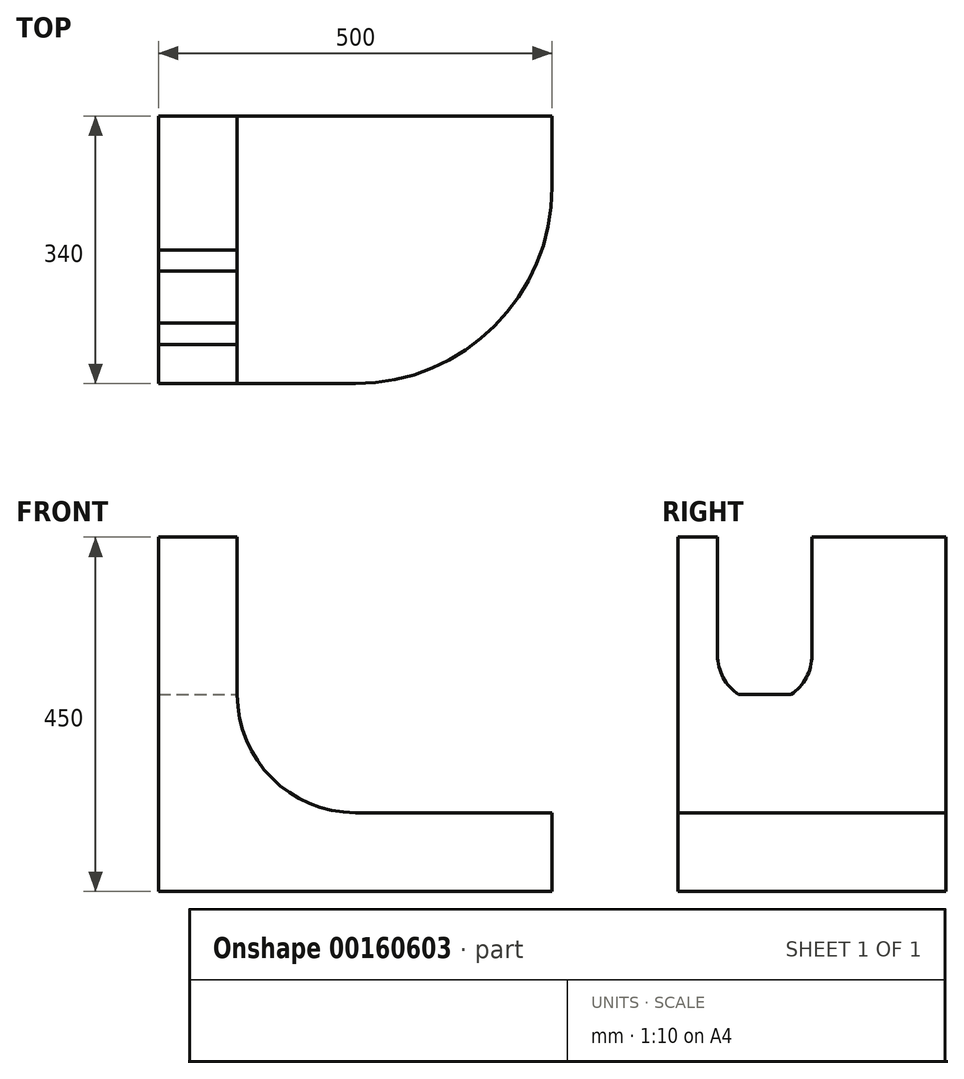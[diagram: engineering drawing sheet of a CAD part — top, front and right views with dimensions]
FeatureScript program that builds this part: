
annotation { "Feature Type Name" : "Feature", "Feature Type Description" : "" }
export const myFeature = defineFeature(function(context is Context, id is Id, definition is map)
    precondition{}
    {
        {
            var Q0;
            Q0=qCreatedBy(makeId("Front.planeOp"),FACE);
            var sketch = newSketch(context, id + "F0", { "sketchPlane" : qUnion([Q0])});
            skLineSegment(sketch, "E0", {"start": v(0, 0) * mm, "end": v(0, 450) * mm});
            skLineSegment(sketch, "E1", {"start": v(0, 0) * mm, "end": v(500, 0) * mm});
            skLineSegment(sketch, "E2.0", {"start": v(250, 100) * mm, "end": v(500, 100) * mm});
            skLineSegment(sketch, "E3.0", {"start": v(100, 250) * mm, "end": v(100, 450) * mm});
            skLineSegment(sketch, "E4", {"start": v(0, 450) * mm, "end": v(100, 450) * mm});
            skLineSegment(sketch, "E5", {"start": v(500, 100) * mm, "end": v(500, 0) * mm});
            skPoint(sketch, "E6.visualSharp", {"position": v(100, 100) * mm});
            skArc(sketch, "E6.filletArc", {"start": v(100, 250) * mm, "mid": v(143.93, 143.93) * mm, "end": v(250, 100) * mm});
            skSolve(sketch);
        }
        {
            var Q0;
            Q0=makeQuery(id+"F0.imprint","IMPRINT",FACE,{"disambiguationData":[TD([[makeQuery(id+"F0.imprint","IMPRINT",EDGE,{"derivedFrom":sQuery(id+"F0.wireOp",EDGE,"E0")}),-1.0]])]});
            extrude(context, id + "F1", {"entities" : qUnion([Q0]), "oppositeDirection" : true, "depth" : 340 * mm});
        }
        {
            var Q0;
            Q0=makeQuery(id+"F1.opExtrude","CAP_EDGE",EDGE,{"disambiguationData":[OSD([sQuery(id+"F0.wireOp",EDGE,"E5")])],"isStart":true});
            fillet(context, id + "F2", {"entities" : qUnion([Q0]), "radius" : 250 * mm, "tangentPropagation" : true, "allowEdgeOverflow" : false});
        }
        {
            var Q0;
            Q0=makeQuery(id+"F1.opExtrude","SWEPT_FACE",FACE,{"disambiguationData":[OSD([sQuery(id+"F0.wireOp",EDGE,"E3.0")])]});
            var sketch = newSketch(context, id + "F3", { "sketchPlane" : qUnion([Q0])});
            skLineSegment(sketch, "E7", {"start": v(170, 450) * mm, "end": v(170, 300) * mm, "construction": true});
            skLineSegment(sketch, "E8", {"start": v(0, 300) * mm, "end": v(110, 300) * mm, "construction": true});
            skArc(sketch, "E9", {"start": v(50, 300) * mm, "mid": v(110, 240) * mm, "end": v(170, 300) * mm});
            skLineSegment(sketch, "E10", {"start": v(50, 300) * mm, "end": v(50, 450) * mm});
            skPoint(sketch, "E10.startSnap0", {"position": v(55, 300) * mm});
            skLineSegment(sketch, "E11", {"start": v(170, 300) * mm, "end": v(170, 450) * mm});
            skLineSegment(sketch, "E12", {"start": v(50, 450) * mm, "end": v(170, 450) * mm});
            skSolve(sketch);
        }
        {
            var Q0;
            {var subQ1=sQuery(id+"F3.wireOp",EDGE,"E10");Q0=makeQuery(id+"F3.imprint","IMPRINT",FACE,{"disambiguationData":[TD([[makeQuery(id+"F3.imprint","IMPRINT",EDGE,{"derivedFrom":subQ1}),-1.0]])]});}
            var Q1;
            Q1=sQuery(id+"F3.wireOp",EDGE,"E9");
            var Q2;
            Q2=sQuery(id+"F3.wireOp",EDGE,"E11");
            var Q3;
            Q3=sQuery(id+"F3.wireOp",EDGE,"E12");
            var Q4;
            Q4=sQuery(id+"F3.wireOp",EDGE,"E10");
            extrude(context, id + "F4", {"entities" : qUnion([Q0]), "operationType" : NewBodyOperationType.REMOVE, "surfaceEntities" : qUnion([Q1, Q2, Q3, Q4]), "oppositeDirection" : true, "depth" : 277.5 * mm});
        }
    });
